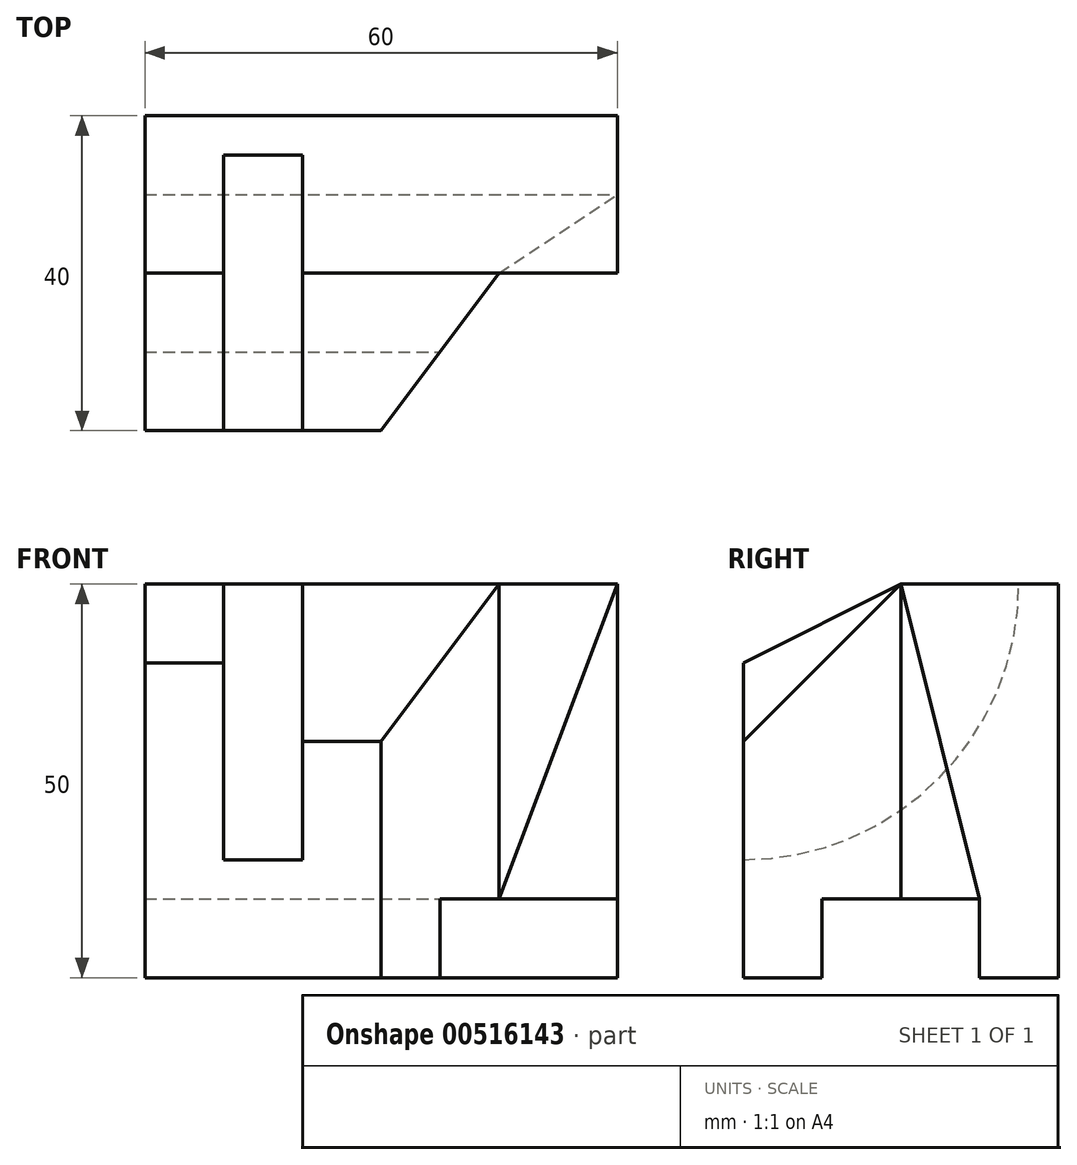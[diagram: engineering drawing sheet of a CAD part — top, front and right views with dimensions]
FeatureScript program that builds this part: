
annotation { "Feature Type Name" : "Feature", "Feature Type Description" : "" }
export const myFeature = defineFeature(function(context is Context, id is Id, definition is map)
    precondition{}
    {
        {
            var Q0;
            Q0=qCreatedBy(makeId("Top.planeOp"),FACE);
            var sketch = newSketch(context, id + "F0", { "sketchPlane" : qUnion([Q0])});
            skLineSegment(sketch, "E0.bottom", {"start": v(0, 0) * mm, "end": v(60, 0) * mm});
            skLineSegment(sketch, "E0.top", {"start": v(0, 40) * mm, "end": v(60, 40) * mm});
            skLineSegment(sketch, "E0.left", {"start": v(0, 0) * mm, "end": v(0, 40) * mm});
            skLineSegment(sketch, "E0.right", {"start": v(60, 0) * mm, "end": v(60, 40) * mm});
            skSolve(sketch);
        }
        {
            var Q0;
            Q0 = qSketchRegion(id + "F0", true);
            extrude(context, id + "F1", {"entities" : qUnion([Q0]), "depth" : 50 * mm, "offsetDistance" : 25 * mm});
        }
        {
            var Q0;
            Q0=makeQuery(id+"F1.opExtrude","CAP_FACE",FACE,{"disambiguationData":[OSD([sQuery(id+"F0.wireOp",EDGE,"E0.bottom"),sQuery(id+"F0.wireOp",EDGE,"E0.top"),sQuery(id+"F0.wireOp",EDGE,"E0.left"),sQuery(id+"F0.wireOp",EDGE,"E0.right")])],"isStart":false});
            var sketch = newSketch(context, id + "F2", { "sketchPlane" : qUnion([Q0])});
            skLineSegment(sketch, "E1.bottom", {"start": v(10, 0) * mm, "end": v(20, 0) * mm});
            skLineSegment(sketch, "E1.top", {"start": v(10, 35) * mm, "end": v(20, 35) * mm});
            skLineSegment(sketch, "E1.left", {"start": v(10, 0) * mm, "end": v(10, 35) * mm});
            skLineSegment(sketch, "E1.right", {"start": v(20, 0) * mm, "end": v(20, 35) * mm});
            skSolve(sketch);
        }
        {
            var Q0;
            Q0=makeQuery(id+"F2.imprint","IMPRINT",FACE,{"disambiguationData":[TD([[makeQuery(id+"F2.imprint","IMPRINT",EDGE,{"derivedFrom":sQuery(id+"F2.wireOp",EDGE,"E1.bottom")}),1.0]])]});
            var Q1;
            Q1=sQuery(id+"F2.wireOp",EDGE,"E1.bottom");
            revolve(context, id + "F3", {"operationType" : NewBodyOperationType.REMOVE, "entities" : qUnion([Q0]), "axis" : qUnion([Q1]), "revolveType" : RevolveType.FULL, "oppositeDirection" : true});
        }
        {
            var Q0;
            Q0=makeQuery(id+"F1.opExtrude","SWEPT_FACE",FACE,{"disambiguationData":[OSD([sQuery(id+"F0.wireOp",EDGE,"E0.bottom")])]});
            var sketch = newSketch(context, id + "F4", { "sketchPlane" : qUnion([Q0])});
            skLineSegment(sketch, "E2", {"start": v(0, 0) * mm, "end": v(0, 40) * mm});
            skLineSegment(sketch, "E3", {"start": v(0, 40) * mm, "end": v(10, 40) * mm});
            skLineSegment(sketch, "E4", {"start": v(20, 0) * mm, "end": v(20, 30) * mm});
            skLineSegment(sketch, "E5", {"start": v(20, 30) * mm, "end": v(60, 30) * mm});
            skSolve(sketch);
        }
        {
            var Q0;
            Q0=makeQuery(id+"F1.opExtrude","SWEPT_FACE",FACE,{"disambiguationData":[OSD([sQuery(id+"F0.wireOp",EDGE,"E0.left")])]});
            var sketch = newSketch(context, id + "F5", { "sketchPlane" : qUnion([Q0])});
            skLineSegment(sketch, "E6", {"start": v(0, 0) * mm, "end": v(0, 40) * mm});
            skLineSegment(sketch, "E7", {"start": v(0, 40) * mm, "end": v(-20, 50) * mm});
            skSolve(sketch);
        }
        {
            var Q0;
            {var subQ0=sQuery(id+"F4.wireOp",EDGE,"E3");Q0=makeQuery(id+"F4.imprint","IMPRINT",FACE,{"disambiguationData":[TD([[makeQuery(id+"F4.imprint","IMPRINT",EDGE,{"derivedFrom":subQ0}),1.0]])]});}
            var Q1;
            Q1=sQuery(id+"F5.wireOp",EDGE,"E7");
            sweep(context, id + "F6", {"operationType" : NewBodyOperationType.REMOVE, "profiles" : qUnion([Q0]), "path" : qUnion([Q1])});
        }
        {
            var Q0;
            Q0=makeQuery(id+"F1.opExtrude","SWEPT_FACE",FACE,{"disambiguationData":[OSD([sQuery(id+"F0.wireOp",EDGE,"E0.bottom")])]});
            var sketch = newSketch(context, id + "F7", { "sketchPlane" : qUnion([Q0])});
            skLineSegment(sketch, "E8", {"start": v(60, 0) * mm, "end": v(60, 30) * mm});
            skLineSegment(sketch, "E9", {"start": v(60, 30) * mm, "end": v(20, 30) * mm});
            skSolve(sketch);
        }
        {
            var Q0;
            Q0=makeQuery(id+"F1.opExtrude","SWEPT_FACE",FACE,{"disambiguationData":[OSD([sQuery(id+"F0.wireOp",EDGE,"E0.right")])]});
            var sketch = newSketch(context, id + "F8", { "sketchPlane" : qUnion([Q0])});
            skLineSegment(sketch, "E10", {"start": v(0, 0) * mm, "end": v(0, 30) * mm});
            skLineSegment(sketch, "E11", {"start": v(0, 30) * mm, "end": v(20, 50) * mm});
            skSolve(sketch);
        }
        {
            var Q0;
            Q0=makeQuery(id+"F1.opExtrude","CAP_FACE",FACE,{"disambiguationData":[OSD([sQuery(id+"F0.wireOp",EDGE,"E0.bottom"),sQuery(id+"F0.wireOp",EDGE,"E0.top"),sQuery(id+"F0.wireOp",EDGE,"E0.left"),sQuery(id+"F0.wireOp",EDGE,"E0.right")])],"isStart":false});
            var sketch = newSketch(context, id + "F9", { "sketchPlane" : qUnion([Q0])});
            skLineSegment(sketch, "E12", {"start": v(20, 0) * mm, "end": v(20, 20) * mm});
            skLineSegment(sketch, "E13", {"start": v(20, 20) * mm, "end": v(45, 20) * mm});
            skLineSegment(sketch, "E14", {"start": v(45, 20) * mm, "end": v(30, 0) * mm});
            skLineSegment(sketch, "E15", {"start": v(30, 0) * mm, "end": v(0, 0) * mm});
            skLineSegment(sketch, "E16", {"start": v(0, 0) * mm, "end": v(45, 0) * mm});
            skLineSegment(sketch, "E17", {"start": v(45, 0) * mm, "end": v(45, 20) * mm});
            skSolve(sketch);
        }
        {
            var Q0;
            {var subQ0=sQuery(id+"F9.wireOp",EDGE,"E14");Q0=makeQuery(id+"F9.imprint","IMPRINT",FACE,{"disambiguationData":[TD([[makeQuery(id+"F9.imprint","IMPRINT",EDGE,{"derivedFrom":subQ0}),1.0]])]});}
            extrude(context, id + "F10", {"entities" : qUnion([Q0]), "operationType" : NewBodyOperationType.REMOVE, "endBound" : BoundingType.THROUGH_ALL, "oppositeDirection" : true, "depth" : 25 * mm, "offsetDistance" : 25 * mm});
        }
        {
            var Q0;
            Q0=makeQuery(id+"F1.opExtrude","CAP_FACE",FACE,{"disambiguationData":[OSD([sQuery(id+"F0.wireOp",EDGE,"E0.bottom"),sQuery(id+"F0.wireOp",EDGE,"E0.top"),sQuery(id+"F0.wireOp",EDGE,"E0.left"),sQuery(id+"F0.wireOp",EDGE,"E0.right")])],"isStart":false});
            var sketch = newSketch(context, id + "F11", { "sketchPlane" : qUnion([Q0])});
            skLineSegment(sketch, "E18", {"start": v(45, 20) * mm, "end": v(60, 20) * mm});
            skSolve(sketch);
        }
        {
            var Q0;
            Q0 = qSketchRegion(id + "F11", true);
            var Q1;
            {var subQ0=sQuery(id+"F11.wireOp",EDGE,"E18");Q1=makeQuery(id+"F11.imprint","IMPRINT",FACE,{"disambiguationData":[TD([[makeQuery(id+"F11.imprint","IMPRINT",EDGE,{"derivedFrom":subQ0}),-1.0]])]});}
            extrude(context, id + "F12", {"entities" : qUnion([Q0, Q1]), "operationType" : NewBodyOperationType.REMOVE, "endBound" : BoundingType.THROUGH_ALL, "oppositeDirection" : true, "depth" : 25 * mm, "offsetDistance" : 25 * mm});
        }
        {
            var Q0;
            {var subQ0=sQuery(id+"F7.wireOp",EDGE,"E9");Q0=makeQuery(id+"F7.imprint","IMPRINT",FACE,{"disambiguationData":[TD([[makeQuery(id+"F7.imprint","IMPRINT",EDGE,{"derivedFrom":subQ0}),-1.0]])]});}
            var Q1;
            Q1=sQuery(id+"F8.wireOp",EDGE,"E11");
            sweep(context, id + "F13", {"operationType" : NewBodyOperationType.REMOVE, "profiles" : qUnion([Q0]), "path" : qUnion([Q1])});
        }
        {
            var Q0;
            Q0=makeQuery(id+"F1.opExtrude","SWEPT_FACE",FACE,{"disambiguationData":[OSD([sQuery(id+"F0.wireOp",EDGE,"E0.right")])]});
            var sketch = newSketch(context, id + "F14", { "sketchPlane" : qUnion([Q0])});
            skLineSegment(sketch, "E19", {"start": v(0, 0) * mm, "end": v(10, 0) * mm});
            skLineSegment(sketch, "E20", {"start": v(10, 0) * mm, "end": v(10, 10) * mm});
            skLineSegment(sketch, "E21", {"start": v(10, 10) * mm, "end": v(30, 10) * mm});
            skLineSegment(sketch, "E22", {"start": v(30, 10) * mm, "end": v(30, 0) * mm});
            skLineSegment(sketch, "E23", {"start": v(10, 0) * mm, "end": v(30, 0) * mm});
            skSolve(sketch);
        }
        {
            var Q0;
            {var subQ0=sQuery(id+"F14.wireOp",EDGE,"E22");Q0=makeQuery(id+"F14.imprint","IMPRINT",FACE,{"disambiguationData":[TD([[makeQuery(id+"F14.imprint","IMPRINT",EDGE,{"derivedFrom":subQ0}),-1.0]])]});}
            var Q1;
            {var subQ0=sQuery(id+"F14.wireOp",EDGE,"E20");Q1=makeQuery(id+"F14.imprint","IMPRINT",FACE,{"disambiguationData":[TD([[makeQuery(id+"F14.imprint","IMPRINT",EDGE,{"derivedFrom":subQ0}),-1.0]])]});}
            extrude(context, id + "F15", {"entities" : qUnion([Q0, Q1]), "operationType" : NewBodyOperationType.REMOVE, "endBound" : BoundingType.THROUGH_ALL, "oppositeDirection" : true, "depth" : 25 * mm, "offsetDistance" : 25 * mm});
        }
        {
            var Q0;
            Q0=makeQuery(id+"F15.boolean.opBoolean","COPY",FACE,{"derivedFrom":makeQuery(id+"F15.opExtrude","SWEPT_FACE",FACE,{"disambiguationData":[OSD([sQuery(id+"F14.wireOp",EDGE,"E21")])]})});
            var sketch = newSketch(context, id + "F16", { "sketchPlane" : qUnion([Q0])});
            skLineSegment(sketch, "E24", {"start": v(45, -20) * mm, "end": v(60, -30) * mm});
            skSolve(sketch);
        }
        {
            var Q0;
            Q0=makeQuery(id+"F1.opExtrude","SWEPT_FACE",FACE,{"disambiguationData":[OSD([sQuery(id+"F0.wireOp",EDGE,"E0.right")])]});
            var sketch = newSketch(context, id + "F17", { "sketchPlane" : qUnion([Q0])});
            skLineSegment(sketch, "E25", {"start": v(30, 10) * mm, "end": v(20, 50) * mm});
            skSolve(sketch);
        }
        {
            var Q0;
            Q0=makeQuery(id+"F16.imprint","IMPRINT",FACE,{"disambiguationData":[TD([[makeQuery(id+"F16.imprint","IMPRINT",EDGE,{"derivedFrom":sQuery(id+"F16.wireOp",EDGE,"E24")}),1.0]])]});
            var Q1;
            Q1=sQuery(id+"F17.wireOp",EDGE,"E25");
            sweep(context, id + "F18", {"operationType" : NewBodyOperationType.REMOVE, "profiles" : qUnion([Q0]), "path" : qUnion([Q1])});
        }
        {
            var Q0;
            Q0 = qSketchRegion(id + "F14", true);
            var Q1;
            {var subQ0=sQuery(id+"F14.wireOp",EDGE,"E20");Q1=makeQuery(id+"F14.imprint","IMPRINT",FACE,{"disambiguationData":[TD([[makeQuery(id+"F14.imprint","IMPRINT",EDGE,{"derivedFrom":subQ0}),-1.0]])]});}
            extrude(context, id + "F19", {"entities" : qUnion([Q0, Q1]), "operationType" : NewBodyOperationType.REMOVE, "endBound" : BoundingType.THROUGH_ALL, "oppositeDirection" : true, "depth" : 25 * mm, "offsetDistance" : 25 * mm});
        }
    });
